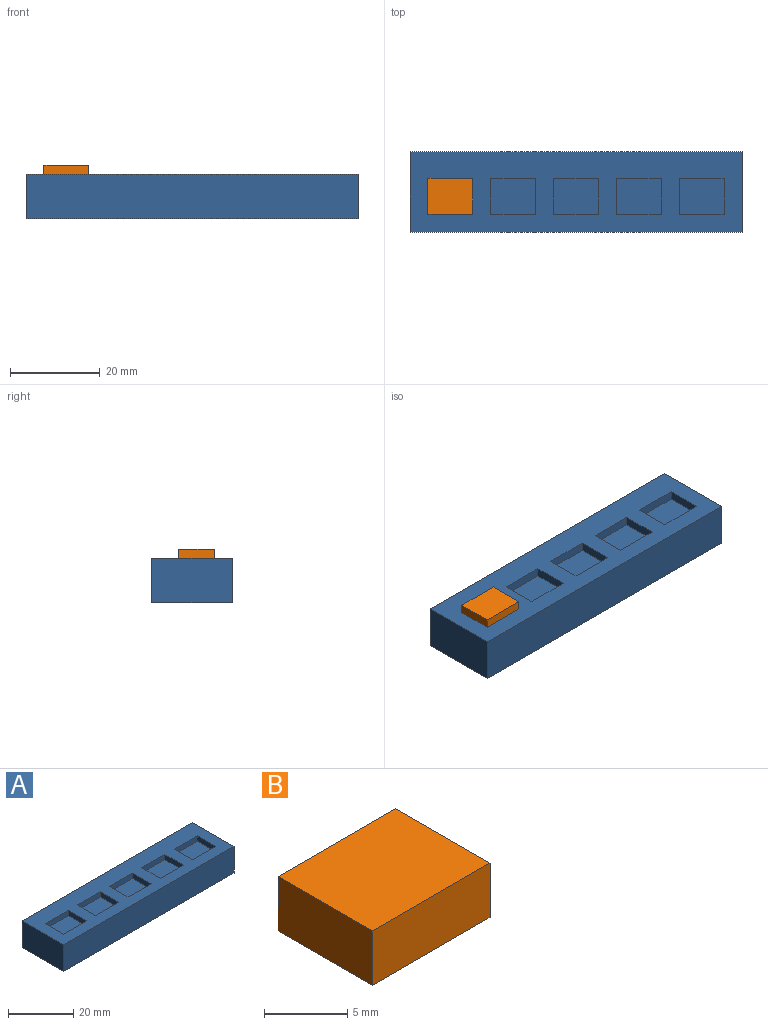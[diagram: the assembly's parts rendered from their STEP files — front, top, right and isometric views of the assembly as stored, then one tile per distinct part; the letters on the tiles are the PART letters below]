
ASSEMBLY  parts=2 mates=1
PART A: 31 faces, bbox 74x18x10 mm
  f0: plane 74x18mm, normal (0,0,1), area 932mm2, adj f1,f2,f3,f4,f6,f7,f8,f9
  f1: plane 18x10mm, normal (1,0,0), area 180mm2, adj f0,f2,f4,f5
  f2: plane 74x10mm, normal (0,1,0), area 740mm2, adj f0,f1,f3,f5
  f3: plane 18x10mm, normal (-1,0,0), area 180mm2, adj f0,f2,f4,f5
  f4: plane 74x10mm, normal (0,-1,0), area 740mm2, adj f0,f1,f3,f5
  f5: plane 74x18mm, normal (0,0,-1), area 1332mm2, adj f1,f2,f3,f4
  f6: plane 10x2mm, normal (0,-1,0), area 20mm2, adj f0,f7,f9,f10
  f7: plane 8x2mm, normal (1,0,0), area 16mm2, adj f0,f6,f8,f10
  f8: plane 10x2mm, normal (0,1,0), area 20mm2, adj f0,f7,f9,f10
  f9: plane 8x2mm, normal (-1,0,0), area 16mm2, adj f0,f6,f8,f10
  f10: plane 10x8mm, normal (0,0,1), area 80mm2, adj f6,f7,f8,f9
  f11: plane 10x2mm, normal (0,-1,0), area 20mm2, adj f0,f12,f14,f15
  f12: plane 8x2mm, normal (1,0,0), area 16mm2, adj f0,f11,f13,f15
  f13: plane 10x2mm, normal (0,1,0), area 20mm2, adj f0,f12,f14,f15
  f14: plane 8x2mm, normal (-1,0,0), area 16mm2, adj f0,f11,f13,f15
  f15: plane 10x8mm, normal (0,0,1), area 80mm2, adj f11,f12,f13,f14
  f16: plane 10x2mm, normal (0,-1,0), area 20mm2, adj f0,f17,f19,f20
  f17: plane 8x2mm, normal (1,0,0), area 16mm2, adj f0,f16,f18,f20
  f18: plane 10x2mm, normal (0,1,0), area 20mm2, adj f0,f17,f19,f20
  f19: plane 8x2mm, normal (-1,0,0), area 16mm2, adj f0,f16,f18,f20
  f20: plane 10x8mm, normal (0,0,1), area 80mm2, adj f16,f17,f18,f19
  f21: plane 10x2mm, normal (0,-1,0), area 20mm2, adj f0,f22,f24,f25
  f22: plane 8x2mm, normal (1,0,0), area 16mm2, adj f0,f21,f23,f25
  f23: plane 10x2mm, normal (0,1,0), area 20mm2, adj f0,f22,f24,f25
  f24: plane 8x2mm, normal (-1,0,0), area 16mm2, adj f0,f21,f23,f25
  f25: plane 10x8mm, normal (0,0,1), area 80mm2, adj f21,f22,f23,f24
  f26: plane 8x2mm, normal (1,0,0), area 16mm2, adj f0,f27,f29,f30
  f27: plane 10x2mm, normal (0,1,0), area 20mm2, adj f0,f26,f28,f30
  f28: plane 8x2mm, normal (-1,0,0), area 16mm2, adj f0,f27,f29,f30
  f29: plane 10x2mm, normal (0,-1,0), area 20mm2, adj f0,f26,f28,f30
  f30: plane 10x8mm, normal (0,0,1), area 80mm2, adj f26,f27,f28,f29
PART B: 6 faces, bbox 10x8x4 mm
  f0: plane 8x4mm, normal (-1,0,0), area 32mm2, adj f1,f3,f4,f5
  f1: plane 10x4mm, normal (0,-1,0), area 40mm2, adj f0,f2,f4,f5
  f2: plane 8x4mm, normal (1,0,0), area 32mm2, adj f1,f3,f4,f5
  f3: plane 10x4mm, normal (0,1,0), area 40mm2, adj f0,f2,f4,f5
  f4: plane 10x8mm, normal (0,0,1), area 80mm2, adj f0,f1,f2,f3
  f5: plane 10x8mm, normal (0,0,-1), area 80mm2, adj f0,f1,f2,f3
PLACE A at identity fixed
PLACE B at identity
MATE fastened A.f30 <-> B.f5  axis (0,0,1) through (-28,-1,8)mm
